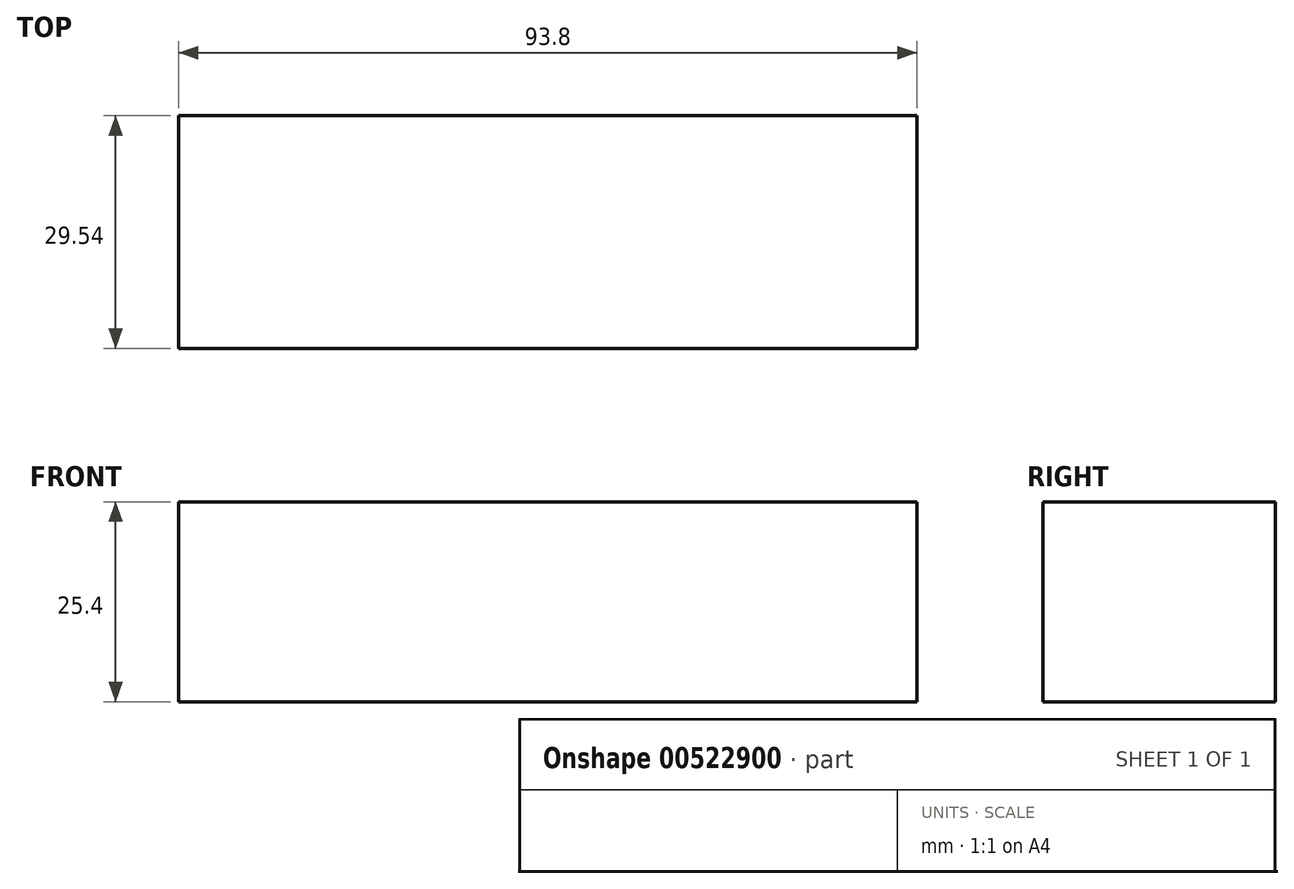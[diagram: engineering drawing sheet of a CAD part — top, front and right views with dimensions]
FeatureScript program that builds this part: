
annotation { "Feature Type Name" : "Feature", "Feature Type Description" : "" }
export const myFeature = defineFeature(function(context is Context, id is Id, definition is map)
    precondition{}
    {
        {
            var Q0;
            Q0=qCreatedBy(makeId("Top.planeOp"),FACE);
            var sketch = newSketch(context, id + "F0", { "sketchPlane" : qUnion([Q0])});
            skLineSegment(sketch, "E0.bottom", {"start": v(-60.15, 47.37) * mm, "end": v(33.65, 47.37) * mm});
            skLineSegment(sketch, "E0.top", {"start": v(-60.15, 17.83) * mm, "end": v(33.65, 17.83) * mm});
            skLineSegment(sketch, "E0.left", {"start": v(-60.15, 47.37) * mm, "end": v(-60.15, 17.83) * mm});
            skLineSegment(sketch, "E0.right", {"start": v(33.65, 47.37) * mm, "end": v(33.65, 17.83) * mm});
            skLineSegment(sketch, "E1.bottom", {"start": v(33.65, 23.93) * mm, "end": v(52.65, 23.93) * mm});
            skLineSegment(sketch, "E1.top", {"start": v(33.65, -29.33) * mm, "end": v(52.65, -29.33) * mm});
            skLineSegment(sketch, "E1.left", {"start": v(33.65, 23.93) * mm, "end": v(33.65, -29.33) * mm});
            skLineSegment(sketch, "E1.right", {"start": v(52.65, 23.93) * mm, "end": v(52.65, -29.33) * mm});
            skSolve(sketch);
        }
        {
            var Q0;
            Q0=makeQuery(id+"F0.imprint","IMPRINT",FACE,{"disambiguationData":[TD([[makeQuery(id+"F0.imprint","IMPRINT",EDGE,{"derivedFrom":sQuery(id+"F0.wireOp",EDGE,"E0.bottom")}),-1.0]])]});
            extrude(context, id + "F1", {"entities" : qUnion([Q0]), "depth" : 25.4 * mm, "offsetDistance" : 25.4 * mm});
        }
    });
